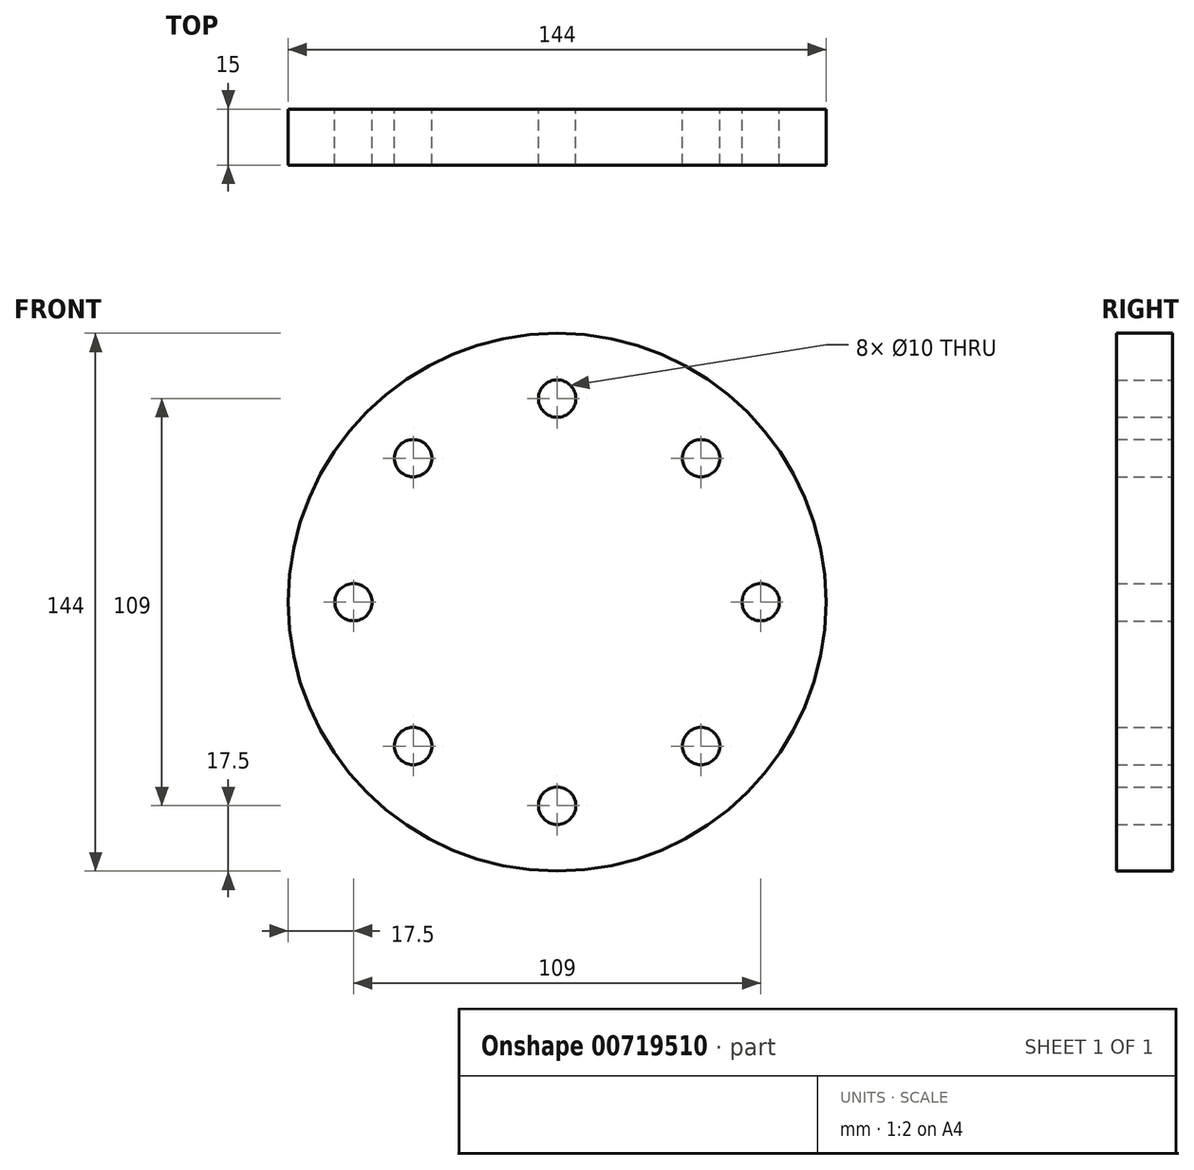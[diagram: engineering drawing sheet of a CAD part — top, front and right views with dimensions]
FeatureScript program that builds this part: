
annotation { "Feature Type Name" : "Feature", "Feature Type Description" : "" }
export const myFeature = defineFeature(function(context is Context, id is Id, definition is map)
    precondition{}
    {
        {
            var Q0;
            Q0=qCreatedBy(makeId("Front.planeOp"),FACE);
            var sketch = newSketch(context, id + "F0", { "sketchPlane" : qUnion([Q0])});
            skCircle(sketch, "E0", {"center": v(0, 0) * mm, "radius": 54.5 * mm, "construction": true});
            skCircle(sketch, "E1", {"center": v(0, 0) * mm, "radius": 72 * mm});
            skCircle(sketch, "E2", {"center": v(0, 54.5) * mm, "radius": 5 * mm});
            skCircle(sketch, "E3.1.0", {"center": v(-38.54, 38.54) * mm, "radius": 5 * mm});
            skCircle(sketch, "E3.2.0", {"center": v(-54.5, 0) * mm, "radius": 5 * mm});
            skCircle(sketch, "E3.3.0", {"center": v(-38.54, -38.54) * mm, "radius": 5 * mm});
            skCircle(sketch, "E3.4.0", {"center": v(0, -54.5) * mm, "radius": 5 * mm});
            skCircle(sketch, "E3.5.0", {"center": v(38.54, -38.54) * mm, "radius": 5 * mm});
            skCircle(sketch, "E3.6.0", {"center": v(54.5, 0) * mm, "radius": 5 * mm});
            skCircle(sketch, "E3.7.0", {"center": v(38.54, 38.54) * mm, "radius": 5 * mm});
            skSolve(sketch);
        }
        {
            var Q0;
            Q0=makeQuery(id+"F0.imprint","IMPRINT",FACE,{"disambiguationData":[TD([[makeQuery(id+"F0.imprint","IMPRINT",EDGE,{"derivedFrom":sQuery(id+"F0.wireOp",EDGE,"E1")}),1.0]])]});
            extrude(context, id + "F1", {"entities" : qUnion([Q0]), "endBound" : BoundingType.SYMMETRIC, "depth" : 15 * mm, "offsetDistance" : 25 * mm});
        }
    });
